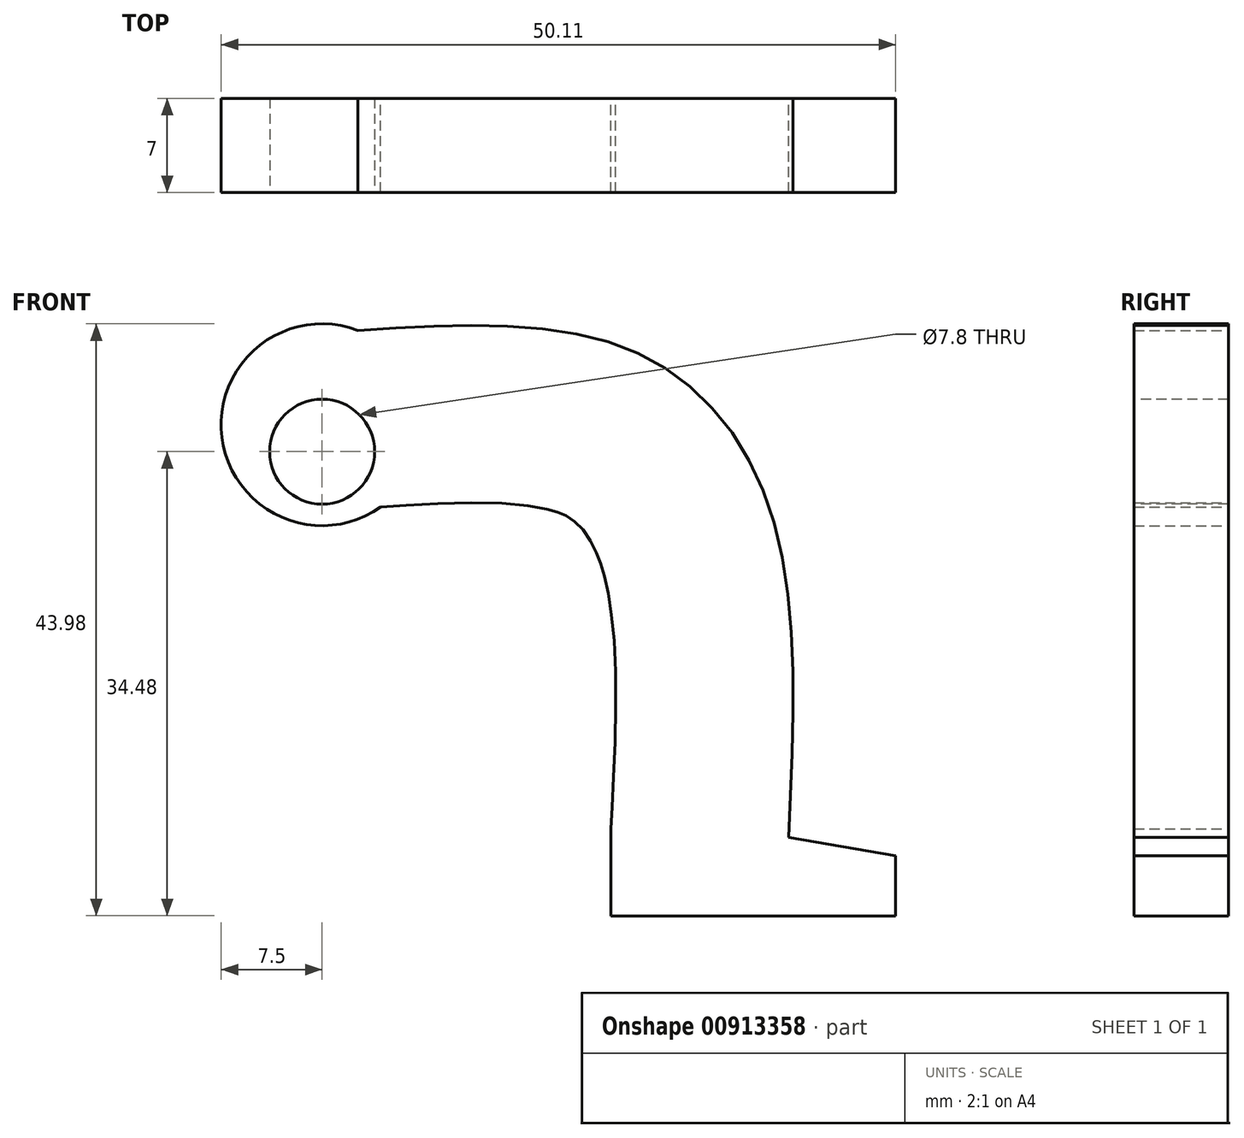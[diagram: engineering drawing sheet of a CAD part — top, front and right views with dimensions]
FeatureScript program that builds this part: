
annotation { "Feature Type Name" : "Feature", "Feature Type Description" : "" }
export const myFeature = defineFeature(function(context is Context, id is Id, definition is map)
    precondition{}
    {
        {
            var Q0;
            Q0=qCreatedBy(makeId("Front.planeOp"),FACE);
            var sketch = newSketch(context, id + "F0", { "sketchPlane" : qUnion([Q0])});
            skArc(sketch, "E0", {"start": v(2.67, 7) * mm, "mid": v(-7.44, -0.95) * mm, "end": v(4.35, -6.11) * mm});
            skFitSpline(sketch, "E1", {"points": [v(2.67, 7) * mm, v(22.81, 5.59) * mm, v(33.17, -6) * mm, v(34.65, -30.66) * mm], "startDerivative": vector(65.15, 3.97) * mm, "endDerivative": vector(-3.48, -72.07) * mm});
            skFitSpline(sketch, "E2.0", {"points": [v(3.47, -6.17) * mm, v(4.83, -6.08) * mm, v(7.43, -5.93) * mm, v(10.93, -5.8) * mm, v(13.89, -5.87) * mm, v(15.78, -6.09) * mm, v(16.75, -6.29) * mm, v(17.19, -6.4) * mm, v(17.47, -6.5) * mm, v(17.7, -6.58) * mm, v(17.94, -6.68) * mm, v(18.21, -6.82) * mm, v(18.52, -7.01) * mm, v(18.82, -7.25) * mm, v(19.13, -7.53) * mm, v(19.43, -7.88) * mm, v(19.75, -8.31) * mm, v(20.06, -8.83) * mm, v(20.31, -9.34) * mm, v(20.5, -9.8) * mm, v(20.64, -10.16) * mm, v(20.77, -10.56) * mm, v(20.95, -11.15) * mm, v(21.16, -12.01) * mm, v(21.37, -13.23) * mm, v(21.6, -15.08) * mm, v(21.78, -17.77) * mm, v(21.8, -21.5) * mm, v(21.68, -25.6) * mm, v(21.54, -28.52) * mm, v(21.46, -30.02) * mm]});
            skLineSegment(sketch, "E3", {"start": v(21.46, -30.02) * mm, "end": v(21.46, -36.48) * mm});
            skLineSegment(sketch, "E4", {"start": v(21.46, -36.48) * mm, "end": v(42.6, -36.48) * mm});
            skLineSegment(sketch, "E5", {"start": v(42.6, -36.48) * mm, "end": v(42.6, -32.03) * mm});
            skLineSegment(sketch, "E6", {"start": v(42.6, -32.03) * mm, "end": v(34.65, -30.66) * mm});
            skSolve(sketch);
        }
        {
            var Q0;
            Q0 = qSketchRegion(id + "F0", true);
            extrude(context, id + "F1", {"entities" : qUnion([Q0]), "depth" : 7 * mm, "offsetDistance" : 25 * mm});
        }
        {
            var Q0;
            Q0=makeQuery(id+"F1.opExtrude","CAP_FACE",FACE,{"disambiguationData":[OSD([sQuery(id+"F0.wireOp",EDGE,"E0"),sQuery(id+"F0.wireOp",EDGE,"E1"),sQuery(id+"F0.wireOp",EDGE,"E2.0"),sQuery(id+"F0.wireOp",EDGE,"E3"),sQuery(id+"F0.wireOp",EDGE,"E4"),sQuery(id+"F0.wireOp",EDGE,"E5"),sQuery(id+"F0.wireOp",EDGE,"E6")])],"isStart":false});
            var sketch = newSketch(context, id + "F2", { "sketchPlane" : qUnion([Q0])});
            skCircle(sketch, "E7", {"center": v(0, -2) * mm, "radius": 3.9 * mm});
            skSolve(sketch);
        }
        {
            var Q0;
            Q0 = qSketchRegion(id + "F2", true);
            extrude(context, id + "F3", {"entities" : qUnion([Q0]), "operationType" : NewBodyOperationType.REMOVE, "oppositeDirection" : true, "depth" : 25 * mm, "offsetDistance" : 25 * mm});
        }
    });
